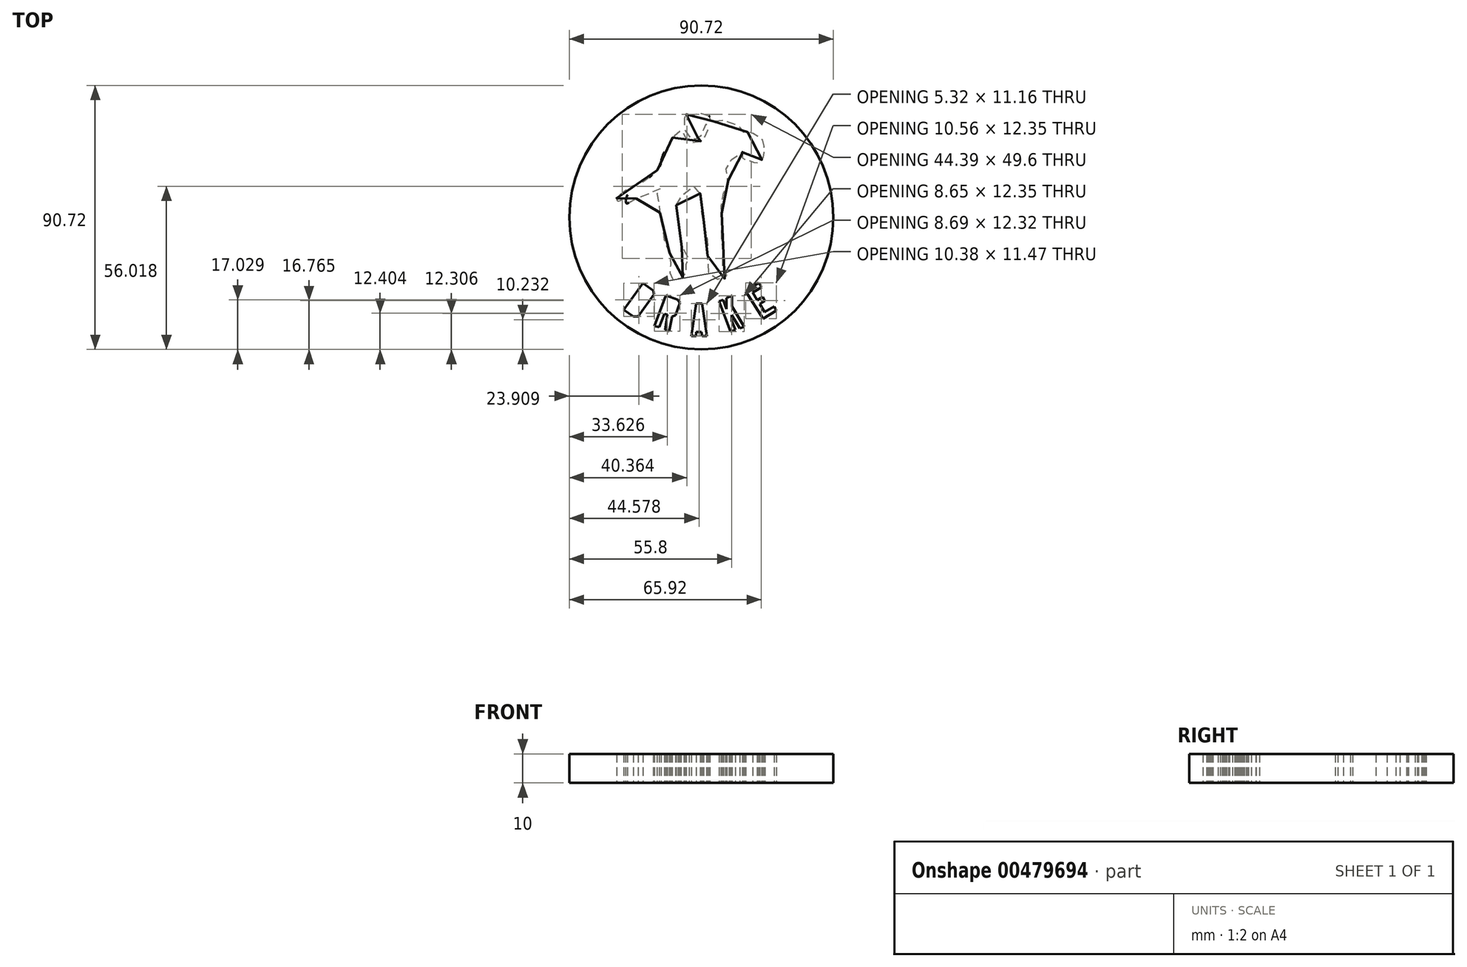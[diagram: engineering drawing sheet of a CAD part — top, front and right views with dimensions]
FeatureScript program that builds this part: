
annotation { "Feature Type Name" : "Feature", "Feature Type Description" : "" }
export const myFeature = defineFeature(function(context is Context, id is Id, definition is map)
    precondition{}
    {
        {
            var Q0;
            Q0=qCreatedBy(makeId("Top.planeOp"),FACE);
            var sketch = newSketch(context, id + "F0", { "sketchPlane" : qUnion([Q0])});
            skCircle(sketch, "E0", {"center": v(0, 0) * mm, "radius": 45.36 * mm});
            skLineSegment(sketch, "E1", {"start": v(-24.27, -31.4) * mm, "end": v(-19.56, -24.85) * mm});
            skLineSegment(sketch, "E2", {"start": v(-19.56, -24.85) * mm, "end": v(-17.98, -25.99) * mm});
            skLineSegment(sketch, "E3", {"start": v(-17.98, -25.99) * mm, "end": v(-22.7, -32.55) * mm});
            skLineSegment(sketch, "E4", {"start": v(-22.7, -32.55) * mm, "end": v(-24.27, -31.4) * mm});
            skLineSegment(sketch, "E5", {"start": v(-11.18, -28.8) * mm, "end": v(-9.17, -29.52) * mm});
            skLineSegment(sketch, "E6", {"start": v(-9.17, -29.52) * mm, "end": v(-10.19, -32.34) * mm});
            skLineSegment(sketch, "E7", {"start": v(-10.19, -32.34) * mm, "end": v(-12.14, -31.64) * mm});
            skLineSegment(sketch, "E8", {"start": v(-12.14, -31.64) * mm, "end": v(-11.18, -28.8) * mm});
            skLineSegment(sketch, "E9", {"start": v(-26.64, -31.7) * mm, "end": v(-20.06, -22.6) * mm});
            skLineSegment(sketch, "E10", {"start": v(-20.06, -22.6) * mm, "end": v(-16.55, -25.14) * mm});
            skLineSegment(sketch, "E11", {"start": v(-16.55, -25.14) * mm, "end": v(-16.26, -26.43) * mm});
            skLineSegment(sketch, "E12", {"start": v(-16.26, -26.43) * mm, "end": v(-21.74, -34.07) * mm});
            skLineSegment(sketch, "E13", {"start": v(-21.74, -34.07) * mm, "end": v(-23.35, -34.07) * mm});
            skLineSegment(sketch, "E14", {"start": v(-23.35, -34.07) * mm, "end": v(-26.64, -31.7) * mm});
            skLineSegment(sketch, "E15", {"start": v(-16.08, -37.28) * mm, "end": v(-12.2, -26.8) * mm});
            skLineSegment(sketch, "E16", {"start": v(-12.2, -26.8) * mm, "end": v(-8.02, -28.34) * mm});
            skLineSegment(sketch, "E17", {"start": v(-8.02, -28.34) * mm, "end": v(-7.39, -29.32) * mm});
            skLineSegment(sketch, "E18", {"start": v(-7.39, -29.32) * mm, "end": v(-8.88, -33.63) * mm});
            skLineSegment(sketch, "E19", {"start": v(-8.88, -33.63) * mm, "end": v(-10.09, -34.07) * mm});
            skLineSegment(sketch, "E20", {"start": v(-10.09, -34.07) * mm, "end": v(-11.05, -39.12) * mm});
            skLineSegment(sketch, "E21", {"start": v(-11.05, -39.12) * mm, "end": v(-12.42, -38.67) * mm});
            skLineSegment(sketch, "E22", {"start": v(-12.42, -38.67) * mm, "end": v(-11.67, -33.45) * mm});
            skLineSegment(sketch, "E23", {"start": v(-11.67, -33.45) * mm, "end": v(-12.69, -33.1) * mm});
            skLineSegment(sketch, "E24", {"start": v(-12.69, -33.1) * mm, "end": v(-14.5, -37.77) * mm});
            skLineSegment(sketch, "E25", {"start": v(-14.5, -37.77) * mm, "end": v(-16.08, -37.28) * mm});
            skLineSegment(sketch, "E26", {"start": v(-1.36, -37.6) * mm, "end": v(-0.77, -34.3) * mm});
            skLineSegment(sketch, "E27", {"start": v(-0.77, -34.3) * mm, "end": v(-0.28, -37.62) * mm});
            skLineSegment(sketch, "E28", {"start": v(-0.28, -37.62) * mm, "end": v(-1.36, -37.6) * mm});
            skLineSegment(sketch, "E29", {"start": v(-3.44, -40.7) * mm, "end": v(-1.72, -40.7) * mm});
            skLineSegment(sketch, "E30", {"start": v(-1.72, -40.7) * mm, "end": v(-1.72, -39.4) * mm});
            skLineSegment(sketch, "E31", {"start": v(-1.72, -39.4) * mm, "end": v(0, -39.4) * mm});
            skLineSegment(sketch, "E32", {"start": v(0, -39.4) * mm, "end": v(0.31, -40.7) * mm});
            skLineSegment(sketch, "E33", {"start": v(0.31, -40.7) * mm, "end": v(1.88, -40.7) * mm});
            skLineSegment(sketch, "E34", {"start": v(1.88, -40.7) * mm, "end": v(0.26, -29.55) * mm});
            skLineSegment(sketch, "E35", {"start": v(0.26, -29.55) * mm, "end": v(-1.72, -29.55) * mm});
            skLineSegment(sketch, "E36", {"start": v(-1.72, -29.55) * mm, "end": v(-3.44, -40.7) * mm});
            skLineSegment(sketch, "E37", {"start": v(10.39, -35.43) * mm, "end": v(11.7, -38.55) * mm});
            skLineSegment(sketch, "E38", {"start": v(11.7, -38.55) * mm, "end": v(10.08, -39.23) * mm});
            skLineSegment(sketch, "E39", {"start": v(10.08, -39.23) * mm, "end": v(6.11, -28.79) * mm});
            skLineSegment(sketch, "E40", {"start": v(6.11, -28.79) * mm, "end": v(7.45, -28.28) * mm});
            skLineSegment(sketch, "E41", {"start": v(7.45, -28.28) * mm, "end": v(8.67, -31.5) * mm});
            skLineSegment(sketch, "E42", {"start": v(8.67, -31.5) * mm, "end": v(8.67, -27.73) * mm});
            skLineSegment(sketch, "E43", {"start": v(8.67, -27.73) * mm, "end": v(10.6, -26.88) * mm});
            skLineSegment(sketch, "E44", {"start": v(10.6, -26.88) * mm, "end": v(10.6, -30.6) * mm});
            skLineSegment(sketch, "E45", {"start": v(10.6, -30.6) * mm, "end": v(14.77, -37.6) * mm});
            skLineSegment(sketch, "E46", {"start": v(14.77, -37.6) * mm, "end": v(13.16, -38.05) * mm});
            skLineSegment(sketch, "E47", {"start": v(13.16, -38.05) * mm, "end": v(10.44, -33.5) * mm});
            skLineSegment(sketch, "E48", {"start": v(10.44, -33.5) * mm, "end": v(10.39, -35.43) * mm});
            skLineSegment(sketch, "E49", {"start": v(21.17, -34.77) * mm, "end": v(25.84, -31.98) * mm});
            skLineSegment(sketch, "E50", {"start": v(25.84, -31.98) * mm, "end": v(25, -30.6) * mm});
            skLineSegment(sketch, "E51", {"start": v(25, -30.6) * mm, "end": v(21.7, -32.57) * mm});
            skLineSegment(sketch, "E52", {"start": v(21.7, -32.57) * mm, "end": v(20.03, -29.78) * mm});
            skLineSegment(sketch, "E53", {"start": v(20.03, -29.78) * mm, "end": v(21.9, -28.66) * mm});
            skLineSegment(sketch, "E54", {"start": v(21.9, -28.66) * mm, "end": v(21.06, -27.27) * mm});
            skLineSegment(sketch, "E55", {"start": v(21.06, -27.27) * mm, "end": v(19.14, -28.42) * mm});
            skLineSegment(sketch, "E56", {"start": v(19.14, -28.42) * mm, "end": v(17.6, -25.84) * mm});
            skLineSegment(sketch, "E57", {"start": v(17.6, -25.84) * mm, "end": v(20.66, -24.01) * mm});
            skLineSegment(sketch, "E58", {"start": v(20.66, -24.01) * mm, "end": v(19.71, -22.42) * mm});
            skLineSegment(sketch, "E59", {"start": v(19.71, -22.42) * mm, "end": v(15.28, -25.4) * mm});
            skLineSegment(sketch, "E60", {"start": v(15.28, -25.4) * mm, "end": v(21.17, -34.77) * mm});
            skFitSpline(sketch, "E61", {"points": [v(-8.6, 4.13) * mm, v(-7.76, 5.25) * mm, v(-6.9, 7.3) * mm, v(-3.2, 10.09) * mm, v(-2.87, 10.59) * mm, v(-2.4, 10.64) * mm, v(-0.49, 8.86) * mm, v(-0.43, 8.1) * mm, v(-0.36, 7.21) * mm, v(0, 5.22) * mm, v(0.27, 4.3) * mm, v(0.27, 3.47) * mm, v(0.2, 3.08) * mm, v(0, 2.37) * mm, v(0.32, 0.9) * mm, v(0.74, -0.37) * mm, v(0.95, -4.61) * mm, v(2.05, -7.86) * mm, v(1.8, -8.76) * mm, v(1.85, -9.76) * mm, v(2.25, -11.2) * mm, v(2.25, -12.9) * mm, v(2.1, -13.75) * mm, v(2.15, -15.3) * mm, v(2.35, -18.25) * mm, v(2.85, -19.95) * mm, v(4.3, -20.95) * mm, v(7.3, -21.2) * mm, v(8.45, -20.85) * mm, v(8.8, -19.9) * mm, v(8.45, -18.6) * mm, v(7.55, -17.25) * mm, v(7.2, -12.55) * mm, v(7.5, -11.1) * mm, v(7.5, -9.46) * mm, v(7.2, -8.76) * mm, v(7.06, -7.14) * mm, v(7.33, -5.43) * mm, v(7.02, -4.11) * mm, v(7.46, -2.97) * mm, v(7.33, -0.65) * mm, v(6.89, 1.76) * mm, v(6.84, 2.77) * mm, v(6.8, 5) * mm, v(7.28, 7.29) * mm, v(8.16, 9.21) * mm, v(8.9, 10.64) * mm, v(9.3, 12.84) * mm, v(9.4, 14.3) * mm, v(8.28, 17.7) * mm, v(9.01, 18.32) * mm, v(10.6, 20.19) * mm, v(12.4, 22.33) * mm, v(14.27, 22.33) * mm, v(14.17, 21.88) * mm, v(14.05, 21.01) * mm, v(14.31, 20.02) * mm, v(15.45, 19.82) * mm, v(16.75, 19.42) * mm, v(18.59, 18.74) * mm, v(19.58, 18.87) * mm, v(20.92, 19.9) * mm, v(21.44, 21.03) * mm, v(21.57, 23.16) * mm, v(21.18, 26.3) * mm, v(19.26, 27.91) * mm, v(16.86, 29.22) * mm, v(15.42, 29.31) * mm, v(14.2, 29.35) * mm, v(14.03, 30.4) * mm, v(11.63, 31.93) * mm, v(9.84, 32.54) * mm, v(6.48, 33.28) * mm, v(3.25, 33.1) * mm, v(2.85, 34.5) * mm, v(2.8, 34.77) * mm, v(1.94, 34.53) * mm, v(0.52, 35.94) * mm, v(-0.95, 35.51) * mm, v(-3.42, 35.27) * mm, v(-5.88, 35.27) * mm, v(-5.82, 33.6) * mm, v(-5.82, 32.19) * mm, v(-5.82, 30.71) * mm, v(-4.34, 27.94) * mm, v(-2.68, 26.96) * mm, v(-0.65, 27.57) * mm, v(0.52, 29.17) * mm, v(1.14, 31.45) * mm, v(1.7, 32.19) * mm, v(2.06, 29.6) * mm, v(0.7, 26.96) * mm, v(-0.58, 25.97) * mm, v(-3.6, 25.72) * mm, v(-4.9, 26.7) * mm, v(-6.3, 29.23) * mm, v(-6.68, 29.85) * mm, v(-8.22, 28.86) * mm, v(-10.25, 27.02) * mm, v(-10.99, 25.72) * mm, v(-11.97, 23.45) * mm, v(-12.84, 22.28) * mm, v(-13.82, 19.2) * mm, v(-14.19, 17.66) * mm, v(-15.91, 15.44) * mm, v(-21.52, 11.44) * mm, v(-24.53, 10.45) * mm, v(-27.89, 7.73) * mm, v(-28.96, 6.97) * mm, v(-29.03, 6.02) * mm, v(-28.33, 5.64) * mm, v(-25.48, 7.6) * mm, v(-25.93, 6.21) * mm, v(-25.55, 4.76) * mm, v(-24.1, 5.9) * mm, v(-22.76, 6.34) * mm, v(-16.5, 8.87) * mm, v(-13.9, 9.95) * mm, v(-15.1, 8.36) * mm, v(-14.66, 4.7) * mm, v(-13.9, -1.38) * mm, v(-13.15, -4.48) * mm, v(-12.9, -7.45) * mm, v(-12.13, -9.42) * mm, v(-11.57, -10.53) * mm, v(-10.76, -12.76) * mm, v(-10.58, -16.5) * mm, v(-10.76, -18.56) * mm, v(-10.85, -19.99) * mm, v(-9.87, -21.06) * mm, v(-7.55, -21.06) * mm, v(-5.77, -20.16) * mm, v(-5.23, -18.74) * mm, v(-5.32, -16.33) * mm, v(-4.25, -14.81) * mm, v(-4.6, -13.56) * mm, v(-5.5, -11.96) * mm, v(-6.84, -9.9) * mm, v(-7.02, -7.85) * mm, v(-7.46, -4.9) * mm, v(-7.9, -1.96) * mm, v(-8, 0.8) * mm, v(-8.6, 4.13) * mm]});
            skSolve(sketch);
        }
        {
            var Q0;
            Q0=makeQuery(id+"F0.imprint","IMPRINT",FACE,{"disambiguationData":[TD([[makeQuery(id+"F0.imprint","IMPRINT",EDGE,{"derivedFrom":sQuery(id+"F0.wireOp",EDGE,"E0")}),1.0]])]});
            extrude(context, id + "F1", {"entities" : qUnion([Q0]), "depth" : 10 * mm});
        }
    });
